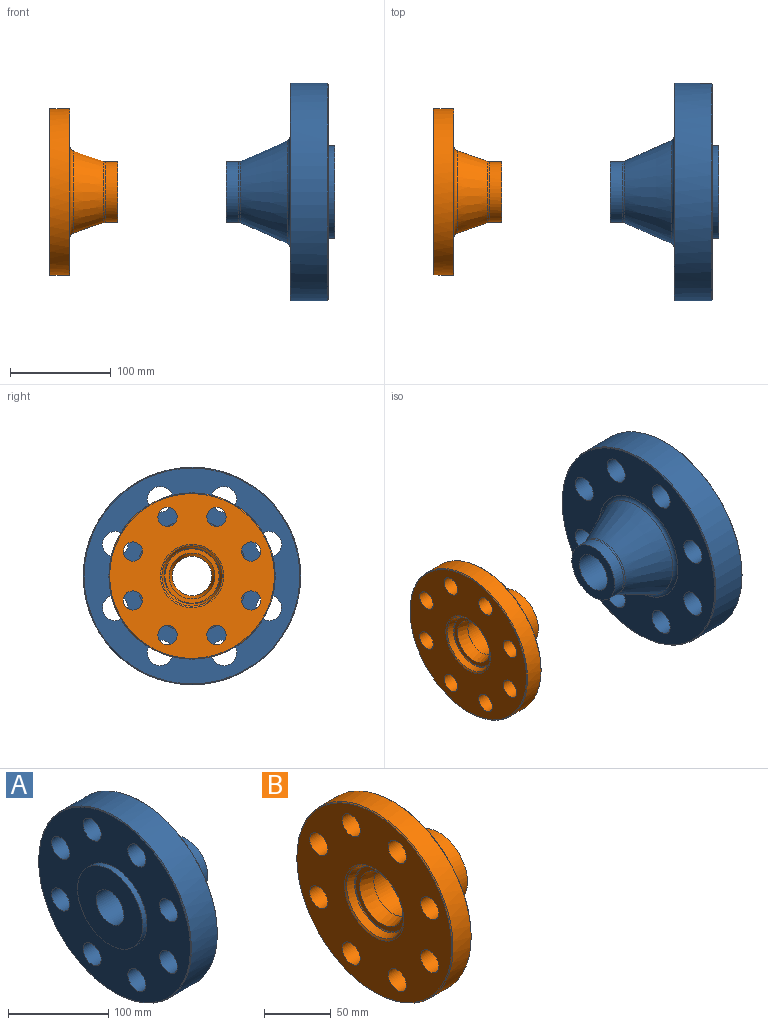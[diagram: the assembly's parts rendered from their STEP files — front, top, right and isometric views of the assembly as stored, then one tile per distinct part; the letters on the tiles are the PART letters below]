
ASSEMBLY  parts=2 mates=1
PART A: 21 faces, bbox 108x216x216 mm
  f0: cylinder r=46mm len=91.99mm, axis (1,0,0), area 1836.1mm2, adj f19,f20
  f1: cylinder r=12.71mm len=38.12mm, axis (1,0,0), area 3043.3mm2, adj f18,f19
  f2: cylinder r=12.71mm len=38.12mm, axis (1,0,0), area 3043.3mm2, adj f18,f19
  f3: cylinder r=12.71mm len=38.12mm, axis (1,0,0), area 3043.3mm2, adj f18,f19
  f4: cylinder r=12.71mm len=38.12mm, axis (1,0,0), area 3043.3mm2, adj f18,f19
  f5: cylinder r=12.71mm len=38.12mm, axis (1,0,0), area 3043.3mm2, adj f18,f19
  f6: cylinder r=12.71mm len=38.12mm, axis (1,0,0), area 3043.3mm2, adj f18,f19
  f7: cylinder r=12.71mm len=38.12mm, axis (1,0,0), area 3043.3mm2, adj f18,f19
  f8: cylinder r=12.71mm len=38.12mm, axis (1,0,0), area 3043.3mm2, adj f18,f19
  f9: torus R=55.46mm, axis (-1,0,0), area 1833mm2, adj f14,f18
  f10: torus R=34.94mm, axis (1,0,0), area 377.1mm2, adj f14,f15
  f11: cone r=107.24mm half-angle=45deg, axis (-1,0,0), area 729.1mm2, adj f13,f18
  f12: cone r=108mm half-angle=45deg, axis (1,0,0), area 729.1mm2, adj f13,f19
  f13: cylinder r=108mm len=216.01mm, axis (1,0,0), area 24833.2mm2, adj f11,f12
  f14: cone r=52.35mm half-angle=23.8deg, axis (-1,0,0), area 13039.4mm2, adj f9,f10
  f15: cylinder r=30.18mm len=60.36mm, axis (1,0,0), area 2327.7mm2, adj f10,f17
  f16: cylinder r=19.62mm len=108mm, axis (1,0,0), area 13317.7mm2, adj f17,f20
  f17: plane 60.36x60.36mm, normal (1,0,0), area 1651.1mm2, adj f15,f16
  f18: plane 214.48x214.48mm, normal (1,0,0), area 22411.5mm2, adj f1,f2,f3,f4,f5,f6,f7,f8
  f19: plane 214.48x214.48mm, normal (-1,0,0), area 25426.2mm2, adj f0,f1,f2,f3,f4,f5,f6,f7
  f20: plane 91.99x91.99mm, normal (-1,0,0), area 5436.8mm2, adj f0,f16
PART B: 24 faces, bbox 68.4x165.2x165.2 mm
  f0: cylinder r=9.53mm len=20.58mm, axis (1,0,0), area 1232.5mm2, adj f22,f23
  f1: cylinder r=9.53mm len=20.58mm, axis (1,0,0), area 1232.5mm2, adj f22,f23
  f2: cylinder r=9.53mm len=20.58mm, axis (1,0,0), area 1232.5mm2, adj f22,f23
  f3: cylinder r=9.53mm len=20.58mm, axis (1,0,0), area 1232.5mm2, adj f22,f23
  f4: cylinder r=9.53mm len=20.58mm, axis (1,0,0), area 1232.5mm2, adj f22,f23
  f5: cylinder r=9.53mm len=20.58mm, axis (1,0,0), area 1232.5mm2, adj f22,f23
  f6: cylinder r=9.53mm len=20.58mm, axis (1,0,0), area 1232.5mm2, adj f22,f23
  f7: cylinder r=9.53mm len=20.58mm, axis (1,0,0), area 1232.5mm2, adj f22,f23
  f8: torus R=45.46mm, axis (-1,0,0), area 1590.1mm2, adj f14,f22
  f9: torus R=34.94mm, axis (1,0,0), area 300.5mm2, adj f14,f15
  f10: cone r=81.83mm half-angle=45deg, axis (-1,0,0), area 556.9mm2, adj f13,f22
  f11: cone r=82.59mm half-angle=45deg, axis (1,0,0), area 556.9mm2, adj f13,f23
  f12: cone r=31.45mm half-angle=65deg, axis (-1,0,0), area 326.8mm2, adj f19,f23
  f13: cylinder r=82.59mm len=165.18mm, axis (1,0,0), area 9890.7mm2, adj f10,f11
  f14: cone r=42.06mm half-angle=19deg, axis (-1,0,0), area 7241.3mm2, adj f8,f9
  f15: cylinder r=30.18mm len=60.36mm, axis (1,0,0), area 2366.9mm2, adj f9,f21
  f16: cylinder r=19.62mm len=49.14mm, axis (1,0,0), area 6058.7mm2, adj f17,f21
  f17: cone r=22.8mm half-angle=15deg, axis (-1,0,0), area 1635.9mm2, adj f16,f20
  f18: torus R=26.96mm, axis (1,0,0), area 160.2mm2, adj f19,f20
  f19: cone r=29.91mm half-angle=20deg, axis (-1,0,0), area 1184.2mm2, adj f12,f18
  f20: plane 53.91x53.91mm, normal (-1,0,0), area 649.3mm2, adj f17,f18
  f21: plane 60.36x60.36mm, normal (1,0,0), area 1651.1mm2, adj f15,f16
  f22: plane 163.66x163.66mm, normal (1,0,0), area 12262.1mm2, adj f0,f1,f2,f3,f4,f5,f6,f7
  f23: plane 163.66x163.66mm, normal (-1,0,0), area 15646.8mm2, adj f0,f1,f2,f3,f4,f5,f6,f7
PLACE A rot(axis=(0,0,1),180deg) t=(277.03,35.5,-41.14)mm
PLACE B t=(-0.48,35.5,-41.14)mm
MATE cylindrical B.f13 <-> A.f13  axis (1,0,0) through (9.81,35.5,-41.14)mm
